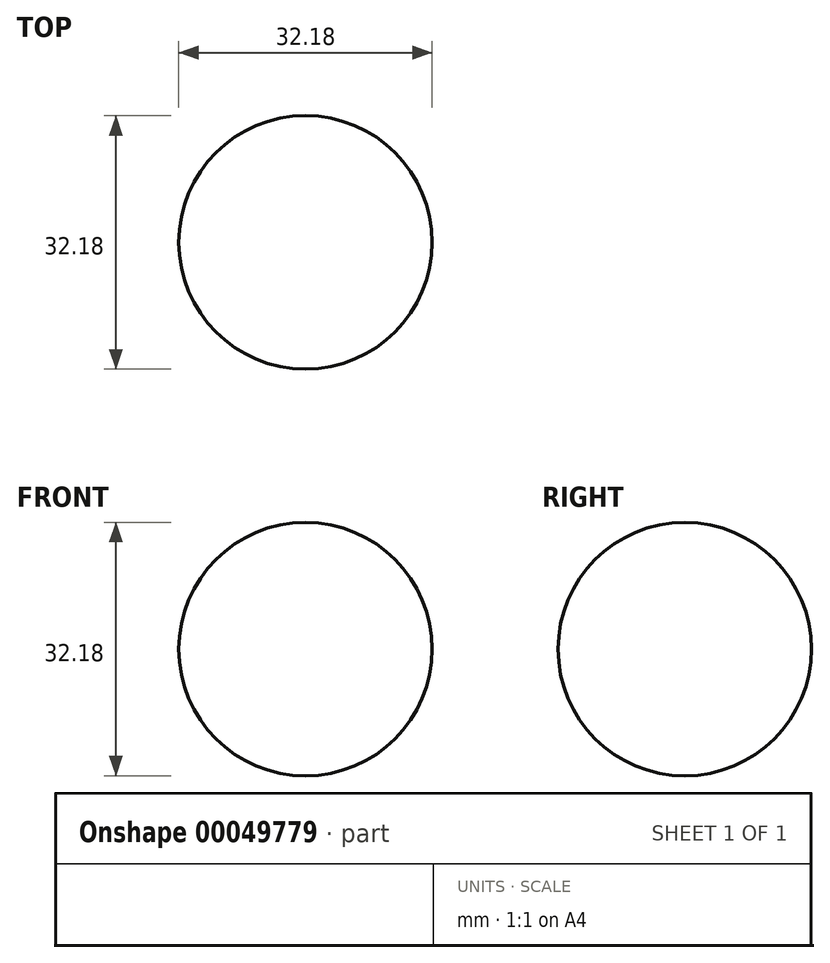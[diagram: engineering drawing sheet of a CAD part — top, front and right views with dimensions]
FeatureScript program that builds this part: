
annotation { "Feature Type Name" : "Feature", "Feature Type Description" : "" }
export const myFeature = defineFeature(function(context is Context, id is Id, definition is map)
    precondition{}
    {
        {
            var Q0;
            Q0=qCreatedBy(makeId("Front.planeOp"),FACE);
            var sketch = newSketch(context, id + "F0", { "sketchPlane" : qUnion([Q0])});
            skArc(sketch, "E0", {"start": v(16.1, 0) * mm, "mid": v(0, 16.1) * mm, "end": v(-16.1, 0) * mm});
            skLineSegment(sketch, "E1", {"start": v(-16.1, 0) * mm, "end": v(16.1, 0) * mm});
            skSolve(sketch);
        }
        {
            var Q0;
            Q0 = qSketchRegion(id + "F0", true);
            var Q1;
            Q1=sQuery(id+"F0.wireOp",EDGE,"E1");
            revolve(context, id + "F1", {"entities" : qUnion([Q0]), "axis" : qUnion([Q1]), "revolveType" : RevolveType.FULL});
        }
    });
